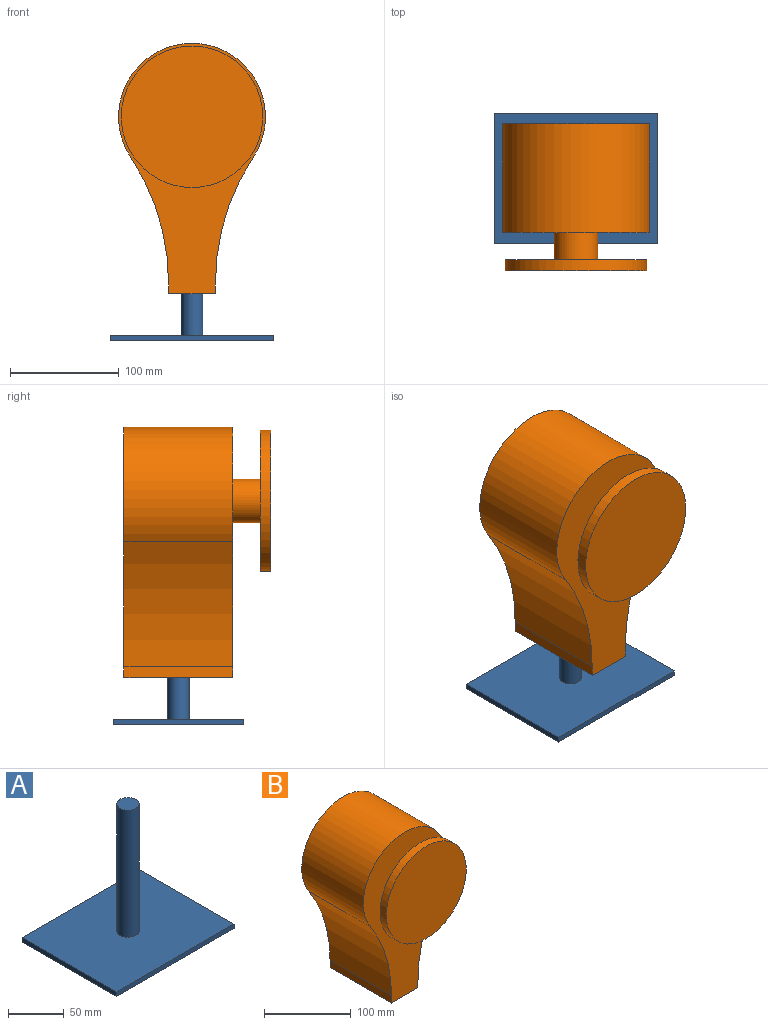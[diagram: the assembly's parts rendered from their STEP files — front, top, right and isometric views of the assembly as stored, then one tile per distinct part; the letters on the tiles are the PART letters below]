
ASSEMBLY  parts=2 mates=1
PART A: 8 faces, bbox 150x120x145 mm
  f0: plane 120x5mm, normal (-1,0,0), area 600mm2, adj f1,f3,f4,f5
  f1: plane 150x5mm, normal (0,-1,0), area 750mm2, adj f0,f2,f4,f5
  f2: plane 120x5mm, normal (1,0,0), area 600mm2, adj f1,f3,f4,f5
  f3: plane 150x5mm, normal (0,1,0), area 750mm2, adj f0,f2,f4,f5
  f4: plane 150x120mm, normal (0,0,1), area 17685.8mm2, adj f0,f1,f2,f3,f6
  f5: plane 150x120mm, normal (0,0,-1), area 18000mm2, adj f0,f1,f2,f3
  f6: cylinder r=10mm len=140mm, axis (0,0,-1), area 8796.5mm2, adj f4,f7
  f7: plane 20x20mm, normal (0,0,1), area 314.2mm2, adj f6
PART B: 14 faces, bbox 135x135x230 mm
  f0: plane 100x10mm, normal (-1,0,0), area 1000mm2, adj f1,f5,f6,f7
  f1: plane 100x43mm, normal (0,0,-1), area 3953.6mm2, adj f0,f2,f6,f7,f12
  f2: plane 100x10mm, normal (1,0,0), area 1000mm2, adj f1,f3,f6,f7
  f3: cylinder r=208.29mm len=115.17mm, axis (0,1,0), area 12203.9mm2, adj f2,f4,f6,f7
  f4: cylinder r=67.5mm len=135mm, axis (0,1,0), area 29115.7mm2, adj f3,f5,f6,f7
  f5: cylinder r=208.29mm len=115.17mm, axis (0,1,0), area 12203.9mm2, adj f0,f4,f6,f7
  f6: plane 230x135mm, normal (0,-1,0), area 18623.3mm2, adj f0,f1,f2,f3,f4,f5,f8
  f7: plane 230x135mm, normal (0,1,0), area 19880mm2, adj f0,f1,f2,f3,f4,f5
  f8: cylinder r=20mm len=40mm, axis (0,1,0), area 3141.6mm2, adj f6,f11
  f9: cylinder r=65mm len=130mm, axis (0,1,0), area 4084.1mm2, adj f10,f11
  f10: plane 130x130mm, normal (0,-1,0), area 13273.2mm2, adj f9
  f11: plane 130x130mm, normal (0,1,0), area 12016.6mm2, adj f8,f9
  f12: cylinder r=10.5mm len=145mm, axis (0,0,-1), area 9566.1mm2, adj f1,f13
  f13: plane 21x21mm, normal (0,0,-1), area 346.4mm2, adj f12
PLACE A t=(-54.84,-10.43,13.17)mm
PLACE B t=(20.16,99.57,218.75)mm
MATE slider B.f12 <-> A.f6  axis (0,0,-1) through (20.16,49.57,56.25)mm
